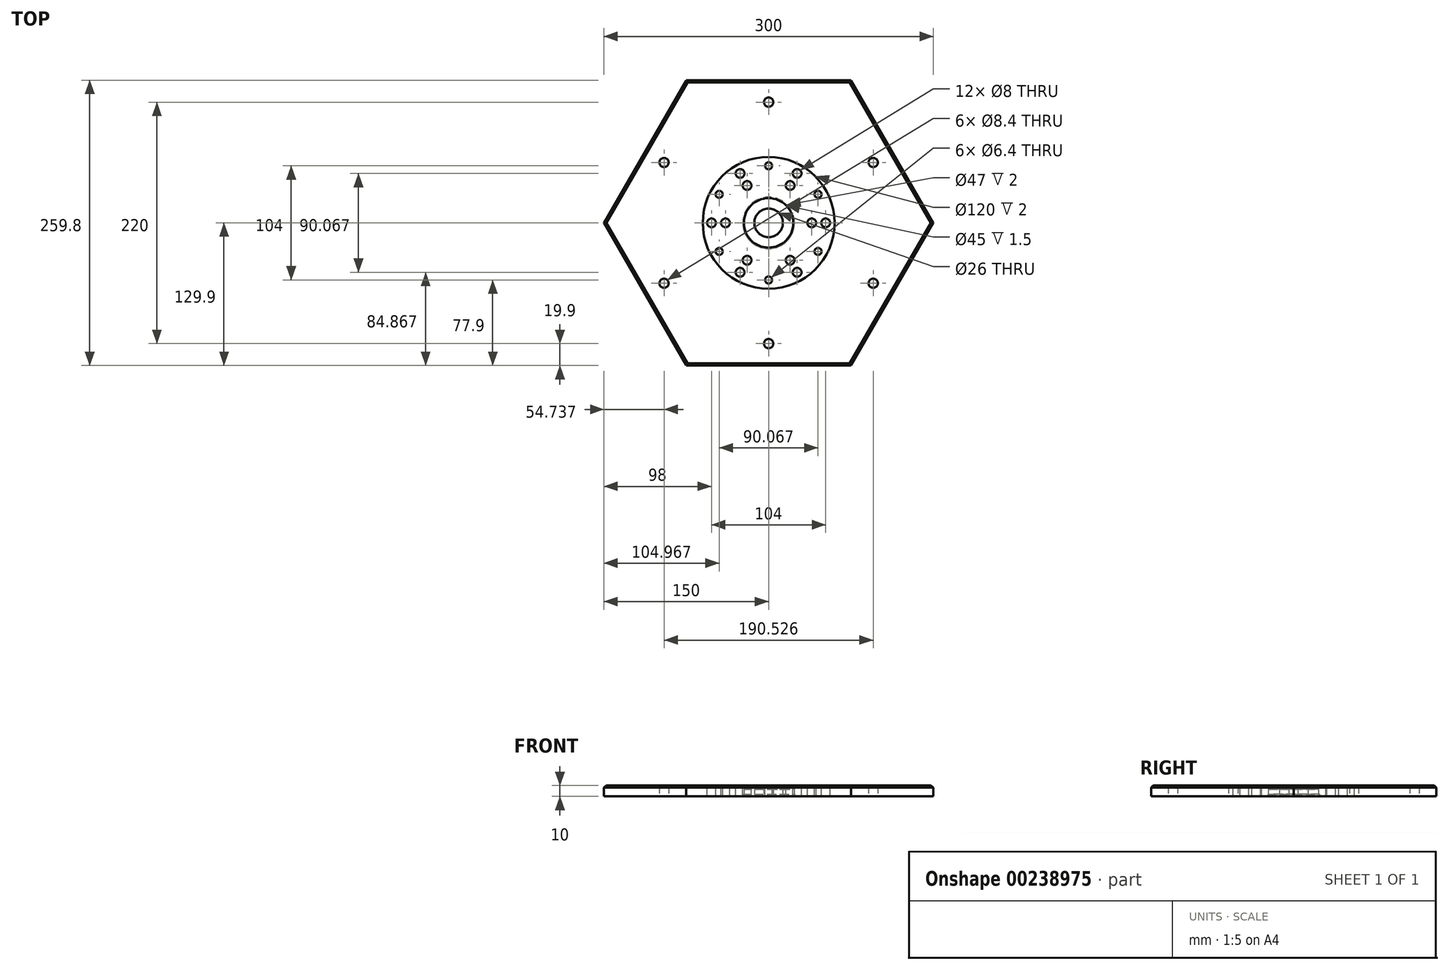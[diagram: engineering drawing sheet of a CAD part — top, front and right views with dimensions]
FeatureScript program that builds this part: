
annotation { "Feature Type Name" : "Feature", "Feature Type Description" : "" }
export const myFeature = defineFeature(function(context is Context, id is Id, definition is map)
    precondition{}
    {
        {
            var Q0;
            Q0=qCreatedBy(makeId("Top.planeOp"),FACE);
            var sketch = newSketch(context, id + "F0", { "sketchPlane" : qUnion([Q0])});
            skCircle(sketch, "E0.cCircle", {"center": v(0, 0) * mm, "radius": 150 * mm, "construction": true});
            skLineSegment(sketch, "E0.0", {"start": v(150, 0) * mm, "end": v(75, -129.9) * mm});
            skLineSegment(sketch, "E0.1", {"start": v(75, -129.9) * mm, "end": v(-75, -129.9) * mm});
            skLineSegment(sketch, "E0.2", {"start": v(-75, -129.9) * mm, "end": v(-150, 0) * mm});
            skLineSegment(sketch, "E0.3", {"start": v(-150, 0) * mm, "end": v(-75, 129.9) * mm});
            skLineSegment(sketch, "E0.4", {"start": v(-75, 129.9) * mm, "end": v(75, 129.9) * mm});
            skLineSegment(sketch, "E0.5", {"start": v(75, 129.9) * mm, "end": v(150, 0) * mm});
            skCircle(sketch, "E1", {"center": v(0, 0) * mm, "radius": 110 * mm, "construction": true});
            skCircle(sketch, "E2", {"center": v(0, 110) * mm, "radius": 4.2 * mm});
            skCircle(sketch, "E3.1.0", {"center": v(-95.26, 55) * mm, "radius": 4.2 * mm});
            skCircle(sketch, "E3.2.0", {"center": v(-95.26, -55) * mm, "radius": 4.2 * mm});
            skCircle(sketch, "E3.3.0", {"center": v(0, -110) * mm, "radius": 4.2 * mm});
            skCircle(sketch, "E3.4.0", {"center": v(95.26, -55) * mm, "radius": 4.2 * mm});
            skCircle(sketch, "E3.5.0", {"center": v(95.26, 55) * mm, "radius": 4.2 * mm});
            skSolve(sketch);
        }
        {
            var Q0;
            Q0=makeQuery(id+"F0.imprint","IMPRINT",FACE,{"disambiguationData":[TD([[makeQuery(id+"F0.imprint","IMPRINT",EDGE,{"derivedFrom":sQuery(id+"F0.wireOp",EDGE,"E0.0")}),-1.0]])]});
            extrude(context, id + "F1", {"entities" : qUnion([Q0]), "depth" : 10 * mm});
        }
        {
            var Q0;
            Q0=qCreatedBy(makeId("Front.planeOp"),FACE);
            var sketch = newSketch(context, id + "F2", { "sketchPlane" : qUnion([Q0])});
            skLineSegment(sketch, "E4", {"start": v(0, 18) * mm, "end": v(0, -22.98) * mm, "construction": true});
            skLineSegment(sketch, "E5", {"start": v(-23.5, 0) * mm, "end": v(8.7, 0) * mm, "construction": true});
            skLineSegment(sketch, "E6", {"start": v(-23.5, -10) * mm, "end": v(0, -10) * mm});
            skLineSegment(sketch, "E7", {"start": v(-60, 18) * mm, "end": v(0, 18) * mm});
            skLineSegment(sketch, "E8", {"start": v(-23.5, 2) * mm, "end": v(-23.5, -10) * mm});
            skLineSegment(sketch, "E9", {"start": v(-23.5, 2) * mm, "end": v(-13, 2) * mm});
            skPoint(sketch, "E10.orphan", {"position": v(-23.5, 0) * mm});
            skLineSegment(sketch, "E11", {"start": v(0, 18) * mm, "end": v(0, -10) * mm});
            skLineSegment(sketch, "E12", {"start": v(-60, 8) * mm, "end": v(-22.5, 8) * mm});
            skLineSegment(sketch, "E13", {"start": v(-60, 18) * mm, "end": v(-60, 8) * mm});
            skLineSegment(sketch, "E14.trimOffspring", {"start": v(-13, 6.5) * mm, "end": v(-13, 2) * mm});
            skLineSegment(sketch, "E15", {"start": v(-13, 6.5) * mm, "end": v(-22.5, 6.5) * mm});
            skLineSegment(sketch, "E16.trimOffspring", {"start": v(-22.5, 8) * mm, "end": v(-22.5, 6.5) * mm});
            skSolve(sketch);
        }
        {
            var Q0;
            Q0=qSketchRegion(id+"F2",true);
            var Q1;
            Q1=sQuery(id+"F2.wireOp",EDGE,"E4");
            revolve(context, id + "F3", {"operationType" : NewBodyOperationType.REMOVE, "entities" : qUnion([Q0]), "axis" : qUnion([Q1]), "revolveType" : RevolveType.FULL, "oppositeDirection" : true});
        }
        {
            var Q0;
            Q0=makeQuery(id+"F3.boolean.opBoolean","COPY",FACE,{"derivedFrom":makeQuery(id+"F3.opRevolve","SWEPT_FACE",FACE,{"disambiguationData":[OSD([sQuery(id+"F2.wireOp",EDGE,"E12")])]})});
            var sketch = newSketch(context, id + "F4", { "sketchPlane" : qUnion([Q0])});
            skPoint(sketch, "E17", {"position": v(0, 0) * mm});
            skLineSegment(sketch, "E18", {"start": v(2.35, 1.36) * mm, "end": v(-10.03, -5.79) * mm, "construction": true});
            skLineSegment(sketch, "E19", {"start": v(0, 0) * mm, "end": v(46.78, 40.67) * mm, "construction": true});
            skCircle(sketch, "E20", {"center": v(0, 0) * mm, "radius": 21.5 * mm, "construction": true});
            skLineSegment(sketch, "E21.anchor2", {"start": v(0, 0) * mm, "end": v(-31, 53.68) * mm, "construction": true});
            skPoint(sketch, "E22", {"position": v(-16.23, -14.1) * mm});
            skCircle(sketch, "E23", {"center": v(0, 0) * mm, "radius": 39.3 * mm, "construction": true});
            skCircle(sketch, "E24", {"center": v(0, 0) * mm, "radius": 52 * mm, "construction": true});
            skPoint(sketch, "E25", {"position": v(-26, 45.03) * mm});
            skPoint(sketch, "E26", {"position": v(-19.65, 34.03) * mm});
            skPoint(sketch, "E27", {"position": v(0, 52) * mm});
            skPoint(sketch, "E28.1.0", {"position": v(-52, 0) * mm});
            skPoint(sketch, "E28.1.1", {"position": v(-39.3, 0) * mm});
            skPoint(sketch, "E28.2.0", {"position": v(-26, -45.03) * mm});
            skPoint(sketch, "E28.2.1", {"position": v(-19.65, -34.03) * mm});
            skPoint(sketch, "E28.3.0", {"position": v(26, -45.03) * mm});
            skPoint(sketch, "E28.3.1", {"position": v(19.65, -34.03) * mm});
            skPoint(sketch, "E28.4.0", {"position": v(52, 0) * mm});
            skPoint(sketch, "E28.4.1", {"position": v(39.3, 0) * mm});
            skPoint(sketch, "E28.5.0", {"position": v(26, 45.03) * mm});
            skPoint(sketch, "E28.5.1", {"position": v(19.65, 34.03) * mm});
            skPoint(sketch, "E29.1.0", {"position": v(-45.03, 26) * mm});
            skPoint(sketch, "E29.2.0", {"position": v(-45.03, -26) * mm});
            skPoint(sketch, "E29.3.0", {"position": v(0, -52) * mm});
            skPoint(sketch, "E29.4.0", {"position": v(45.03, -26) * mm});
            skPoint(sketch, "E29.5.0", {"position": v(45.03, 26) * mm});
            skSolve(sketch);
        }
        {
            var Q0;
            Q0=sQuery(id+"F4.wireOp",VERTEX,"E25");
            var Q1;
            Q1=sQuery(id+"F4.wireOp",VERTEX,"E28.1.0");
            var Q2;
            Q2=sQuery(id+"F4.wireOp",VERTEX,"E28.2.0");
            var Q3;
            Q3=sQuery(id+"F4.wireOp",VERTEX,"E28.3.0");
            var Q4;
            Q4=sQuery(id+"F4.wireOp",VERTEX,"E28.4.0");
            var Q5;
            Q5=sQuery(id+"F4.wireOp",VERTEX,"E28.5.0");
            var Q6;
            Q6=sQuery(id+"F4.wireOp",VERTEX,"E26");
            var Q7;
            Q7=sQuery(id+"F4.wireOp",VERTEX,"E28.1.1");
            var Q8;
            Q8=sQuery(id+"F4.wireOp",VERTEX,"E28.2.1");
            var Q9;
            Q9=sQuery(id+"F4.wireOp",VERTEX,"E28.3.1");
            var Q10;
            Q10=sQuery(id+"F4.wireOp",VERTEX,"E28.4.1");
            var Q11;
            Q11=sQuery(id+"F4.wireOp",VERTEX,"E28.5.1");
            var Q12;
            Q12=makeQuery(id+"F1.opExtrude","SWEPT_BODY",BODY,{"disambiguationData":[OSD([sQuery(id+"F0.wireOp",EDGE,"E0.0"),sQuery(id+"F0.wireOp",EDGE,"E0.1"),sQuery(id+"F0.wireOp",EDGE,"E0.2"),sQuery(id+"F0.wireOp",EDGE,"E0.3"),sQuery(id+"F0.wireOp",EDGE,"E0.4"),sQuery(id+"F0.wireOp",EDGE,"E0.5")])]});
            hole(context, id + "F5", {"style" : HoleStyle.SIMPLE, "endStyle" : HoleEndStyle.BLIND, "holeDiameter" : 8 * mm, "holeDepth" : 15 * mm, "locations" : qUnion([Q0, Q1, Q2, Q3, Q4, Q5, Q6, Q7, Q8, Q9, Q10, Q11]), "scope" : qUnion([Q12]), "tappedDepth" : 12 * mm, "tapClearance" : 3});
        }
        {
            var Q0;
            Q0=sQuery(id+"F4.wireOp",VERTEX,"E27");
            var Q1;
            Q1=sQuery(id+"F4.wireOp",VERTEX,"E29.1.0");
            var Q2;
            Q2=sQuery(id+"F4.wireOp",VERTEX,"E29.2.0");
            var Q3;
            Q3=sQuery(id+"F4.wireOp",VERTEX,"E29.3.0");
            var Q4;
            Q4=sQuery(id+"F4.wireOp",VERTEX,"E29.4.0");
            var Q5;
            Q5=sQuery(id+"F4.wireOp",VERTEX,"E29.5.0");
            var Q6;
            Q6=makeQuery(id+"F1.opExtrude","SWEPT_BODY",BODY,{"disambiguationData":[OSD([sQuery(id+"F0.wireOp",EDGE,"E0.0"),sQuery(id+"F0.wireOp",EDGE,"E0.1"),sQuery(id+"F0.wireOp",EDGE,"E0.2"),sQuery(id+"F0.wireOp",EDGE,"E0.3"),sQuery(id+"F0.wireOp",EDGE,"E0.4"),sQuery(id+"F0.wireOp",EDGE,"E0.5")])]});
            hole(context, id + "F6", {"style" : HoleStyle.SIMPLE, "endStyle" : HoleEndStyle.BLIND, "holeDiameter" : 6.4 * mm, "holeDepth" : 20 * mm, "locations" : qUnion([Q0, Q1, Q2, Q3, Q4, Q5]), "scope" : qUnion([Q6]), "tappedDepth" : 12 * mm, "tapClearance" : 3});
        }
        {
            var Q0;
            Q0=makeQuery(id+"F1.opExtrude","CAP_EDGE",EDGE,{"disambiguationData":[OSD([sQuery(id+"F0.wireOp",EDGE,"E0.1")])],"isStart":false});
            var Q1;
            Q1=makeQuery(id+"F1.opExtrude","CAP_EDGE",EDGE,{"disambiguationData":[OSD([sQuery(id+"F0.wireOp",EDGE,"E0.0")])],"isStart":false});
            var Q2;
            Q2=makeQuery(id+"F1.opExtrude","CAP_EDGE",EDGE,{"disambiguationData":[OSD([sQuery(id+"F0.wireOp",EDGE,"E0.5")])],"isStart":false});
            var Q3;
            Q3=makeQuery(id+"F1.opExtrude","CAP_EDGE",EDGE,{"disambiguationData":[OSD([sQuery(id+"F0.wireOp",EDGE,"E0.4")])],"isStart":false});
            var Q4;
            Q4=makeQuery(id+"F1.opExtrude","CAP_EDGE",EDGE,{"disambiguationData":[OSD([sQuery(id+"F0.wireOp",EDGE,"E0.3")])],"isStart":false});
            var Q5;
            Q5=makeQuery(id+"F1.opExtrude","CAP_EDGE",EDGE,{"disambiguationData":[OSD([sQuery(id+"F0.wireOp",EDGE,"E0.2")])],"isStart":false});
            chamfer(context, id + "F7", {"entities" : qUnion([Q0, Q1, Q2, Q3, Q4, Q5]), "width" : 2 * mm, "tangentPropagation" : true});
        }
    });
